# Revit family: Faucet-Lavatory-KOHLER-Coralais-K-15265
name_source: partatom
category: Plumbing Fixtures
revit_build: Autodesk Revit 2015 (Build: 20140606_1530(x64)
units: mm (PartAtom-declared; Revit-internal decimal feet)

## types (1)
- CP-Polished Chrome
    ADA Compliant = Yes
    Assembly Code = D2010
    CW Connection = Yes
    Cold Water Inlet = Cold Water Inlet
    Date Modified = 05/03/2018
    Default Elevation = 36"
    Description = Widespread bathroom sink faucet with lever handles, less drain and lift rod
    Drain Included = No
    Faucet Hole Spacing = 8"
    Finish = Kohler-Metal-CP-Polished_Chrome
    Flow Rate = 1 GPM
    HW Connection = Yes
    Handle Clearance = 13 1/8"
    Height = 4"
    Hot Water Inlet = Hot Water Inlet
    Length = 4 1/4"
    Manufacturer = KOHLER Co.
    MasterFormat 1995 = 15410
    MasterFormat 2004 = 22.41.39
    Material = Premium Metal Construction
    Model = K-15265-4NDRA-CP
    Pressure = 60.00 psi
    Product Documentation Link = http://www.us.kohler.com
    Product Name = Coralais
    Product Page URL = http://www.us.kohler.com
    Spout Reach = 4 1/4"
    Type = 1
    URL = https://www.us.kohler.com
    Vent Connection = No
    Waste Connection = No
    Waste Water Outlet = Waste Water Outlet
    Width = 8"

## geometry (parser evidence)
native form markers: Sweep x10
no freeform markers — native parametric forms only
